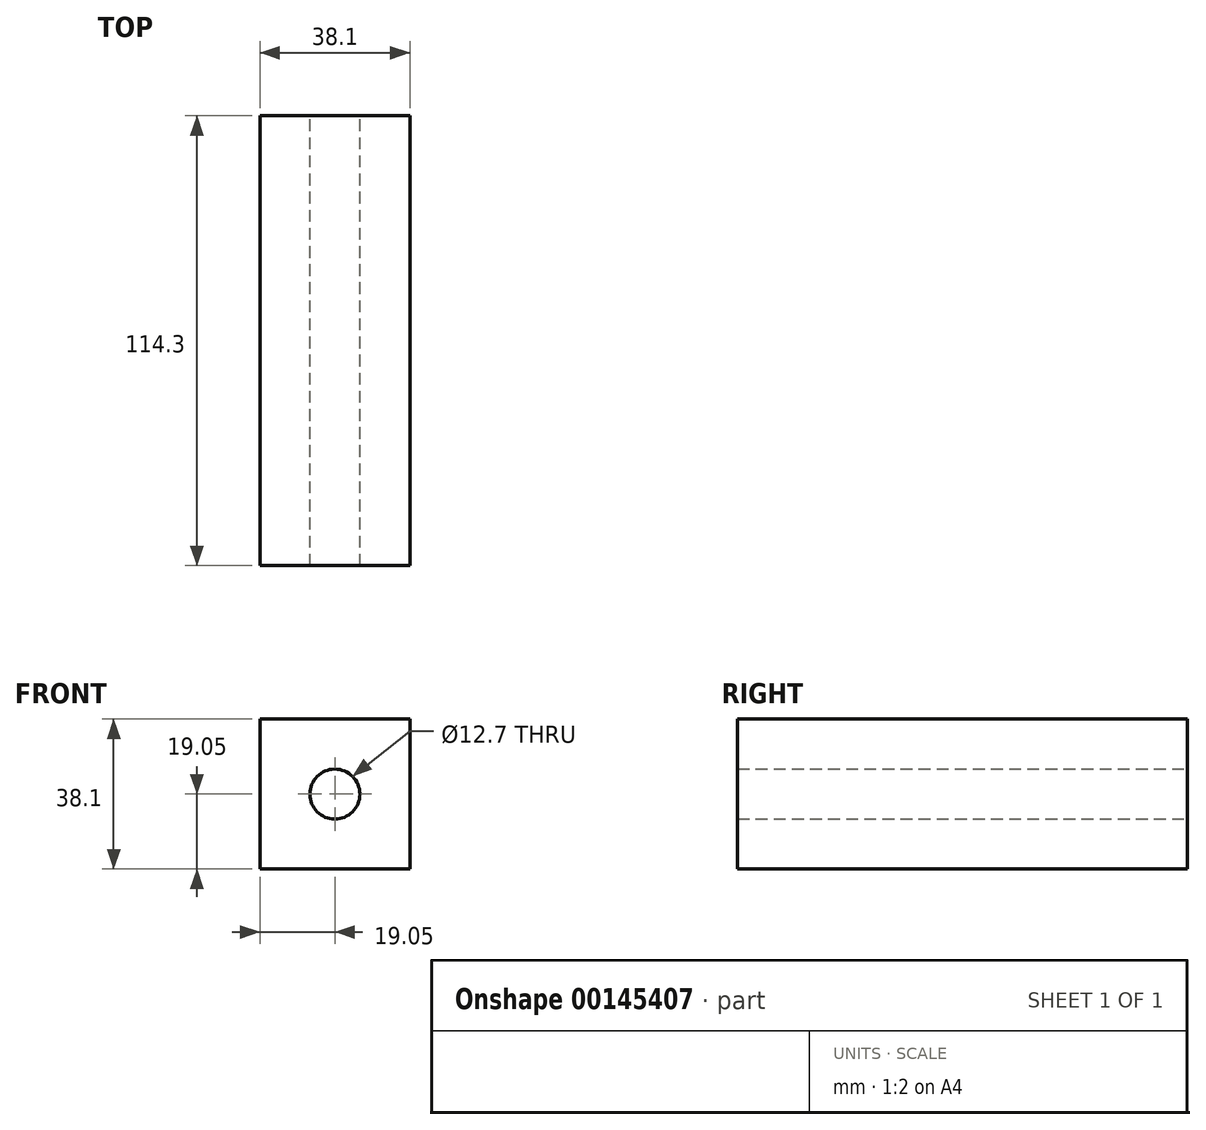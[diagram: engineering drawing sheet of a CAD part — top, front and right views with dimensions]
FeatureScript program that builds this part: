
annotation { "Feature Type Name" : "Feature", "Feature Type Description" : "" }
export const myFeature = defineFeature(function(context is Context, id is Id, definition is map)
    precondition{}
    {
        {
            var Q0;
            Q0=qCreatedBy(makeId("Front.planeOp"),FACE);
            var sketch = newSketch(context, id + "F0", { "sketchPlane" : qUnion([Q0])});
            skLineSegment(sketch, "E0.bottom", {"start": v(-19.05, -19.05) * mm, "end": v(19.05, -19.05) * mm});
            skLineSegment(sketch, "E0.top", {"start": v(-19.05, 19.05) * mm, "end": v(19.05, 19.05) * mm});
            skLineSegment(sketch, "E0.left", {"start": v(-19.05, -19.05) * mm, "end": v(-19.05, 19.05) * mm});
            skLineSegment(sketch, "E0.right", {"start": v(19.05, -19.05) * mm, "end": v(19.05, 19.05) * mm});
            skPoint(sketch, "E0.middle", {"position": v(0, 0) * mm});
            skSolve(sketch);
        }
        {
            var Q0;
            Q0=makeQuery(id+"F0.imprint","IMPRINT",FACE,{"disambiguationData":[TD([[makeQuery(id+"F0.imprint","IMPRINT",EDGE,{"derivedFrom":sQuery(id+"F0.wireOp",EDGE,"E0.bottom")}),1.0]])]});
            extrude(context, id + "F1", {"entities" : qUnion([Q0]), "endBound" : BoundingType.SYMMETRIC, "depth" : 114.3 * mm});
        }
        {
            var Q0;
            Q0=qCreatedBy(makeId("Front.planeOp"),FACE);
            cPlane(context, id + "F2", {"entities" : qUnion([Q0]), "cplaneType" : CPlaneType.OFFSET, "offset" : 152.4 * mm, "oppositeDirection" : true, "width" : 152.4 * mm, "height" : 152.4 * mm});
        }
        {
            var Q0;
            Q0=qCreatedBy(id+"F2.planeOp",FACE);
            var sketch = newSketch(context, id + "F3", { "sketchPlane" : qUnion([Q0])});
            skPoint(sketch, "E1", {"position": v(0, 0) * mm});
            skSolve(sketch);
        }
        {
            var Q0;
            Q0=sQuery(id+"F3.wireOp",VERTEX,"E1");
            var Q1;
            Q1=makeQuery(id+"F1.opExtrude","SWEPT_BODY",BODY,{"disambiguationData":[OSD([sQuery(id+"F0.wireOp",EDGE,"E0.bottom"),sQuery(id+"F0.wireOp",EDGE,"E0.top"),sQuery(id+"F0.wireOp",EDGE,"E0.left"),sQuery(id+"F0.wireOp",EDGE,"E0.right")])]});
            hole(context, id + "F4", {"style" : HoleStyle.SIMPLE, "endStyle" : HoleEndStyle.BLIND, "oppositeDirection" : true, "holeDiameter" : 12.7 * mm, "holeDepth" : 609.6 * mm, "startFromSketch" : true, "locations" : qUnion([Q0]), "scope" : qUnion([Q1])});
        }
    });
